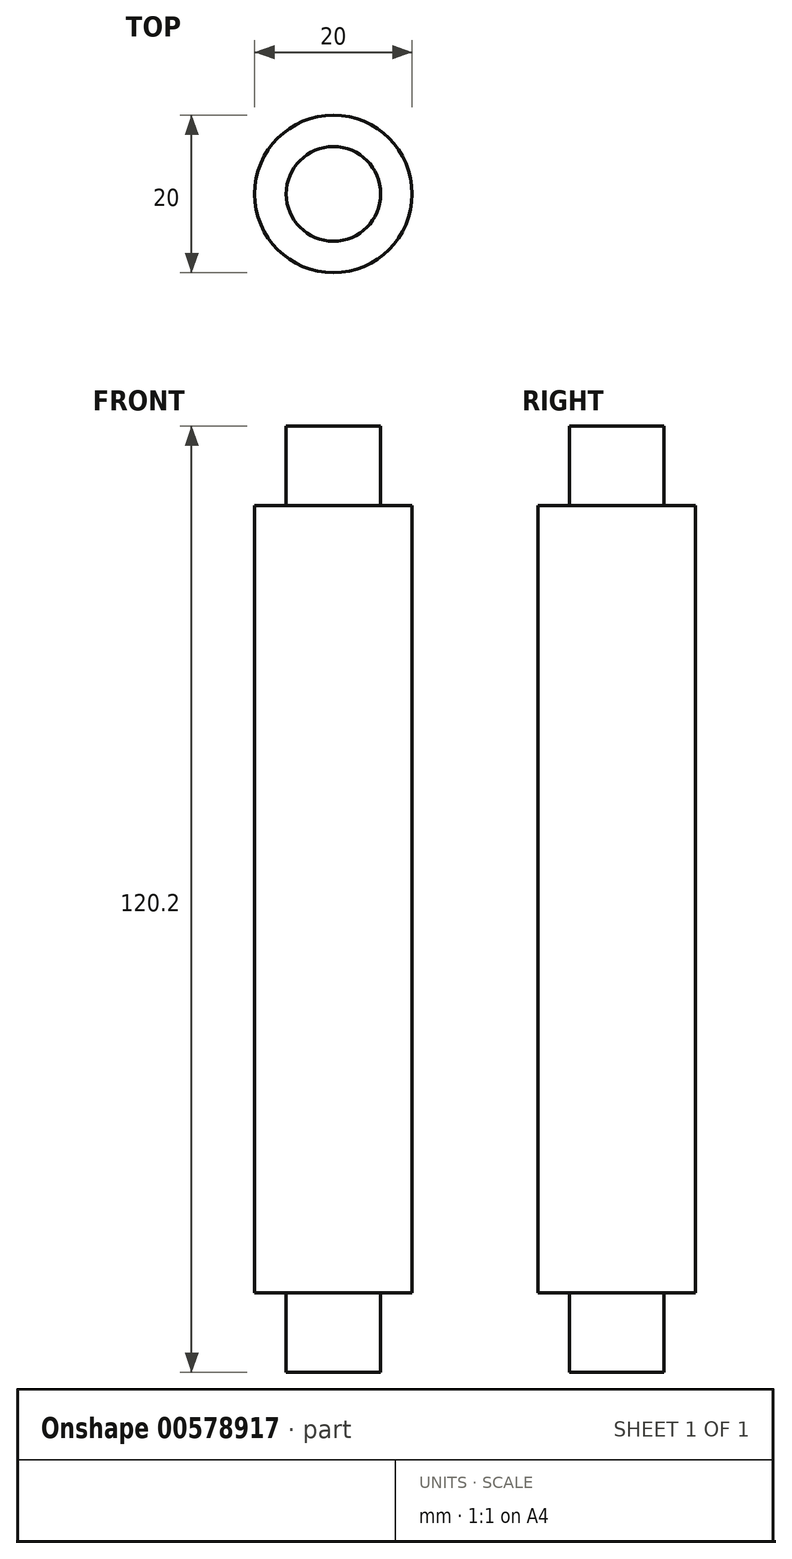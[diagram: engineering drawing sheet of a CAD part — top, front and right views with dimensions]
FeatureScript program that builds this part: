
annotation { "Feature Type Name" : "Feature", "Feature Type Description" : "" }
export const myFeature = defineFeature(function(context is Context, id is Id, definition is map)
    precondition{}
    {
        {
            var Q0;
            Q0=qCreatedBy(makeId("Top.planeOp"),FACE);
            var sketch = newSketch(context, id + "F0", { "sketchPlane" : qUnion([Q0])});
            skCircle(sketch, "E0", {"center": v(0, 0) * mm, "radius": 10 * mm});
            skSolve(sketch);
        }
        {
            var Q0;
            Q0 = qSketchRegion(id + "F0", true);
            extrude(context, id + "F1", {"entities" : qUnion([Q0]), "endBound" : BoundingType.SYMMETRIC, "depth" : 100 * mm, "offsetDistance" : 25 * mm});
        }
        {
            var Q0;
            Q0=makeQuery(id+"F1.opExtrude","CAP_FACE",FACE,{"disambiguationData":[OSD([sQuery(id+"F0.wireOp",EDGE,"E0")])],"isStart":false});
            var sketch = newSketch(context, id + "F2", { "sketchPlane" : qUnion([Q0])});
            skCircle(sketch, "E1", {"center": v(0, 0) * mm, "radius": 6 * mm});
            skSolve(sketch);
        }
        {
            var Q0;
            Q0 = qSketchRegion(id + "F2", true);
            extrude(context, id + "F3", {"entities" : qUnion([Q0]), "operationType" : NewBodyOperationType.ADD, "depth" : 10.1 * mm, "offsetDistance" : 25 * mm});
        }
        {
            var Q0;
            Q0=makeQuery(id+"F1.opExtrude","SWEPT_BODY",BODY,{"disambiguationData":[OSD([sQuery(id+"F0.wireOp",EDGE,"E0")])]});
            var Q1;
            Q1=qCreatedBy(makeId("Top.planeOp"),FACE);
            mirror(context, id + "F4", {"operationType" : NewBodyOperationType.ADD, "entities" : qUnion([Q0]), "mirrorPlane" : qUnion([Q1])});
        }
    });
